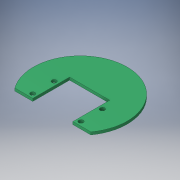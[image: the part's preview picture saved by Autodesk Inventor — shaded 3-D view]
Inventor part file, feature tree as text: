
AUTODESK INVENTOR PART (.ipt)
format: ipt  version: 2016 (Build 200138000, 138)  size: 114,176 bytes
history: native  units: mm
features: extrude x1, sketch x1
ambient origin geometry x8: Origin, YZ Plane, XZ Plane, XY Plane, X Axis, Y Axis, Z Axis, Center Point
bodies: Volumenkörper1 (feature_tree)
feature tree (2):
  extrude  "Extrusion1"  Depth=27.5mm
  sketch  "Skizze1"  dims[d0=3.4mm d5=3.0mm d6=3.0mm d7=32.6mm d8=35.0mm d9=16.0mm d10=2.0mm d11=0.0mm d12=3.0mm d14=20.5mm d15=27.5mm]
